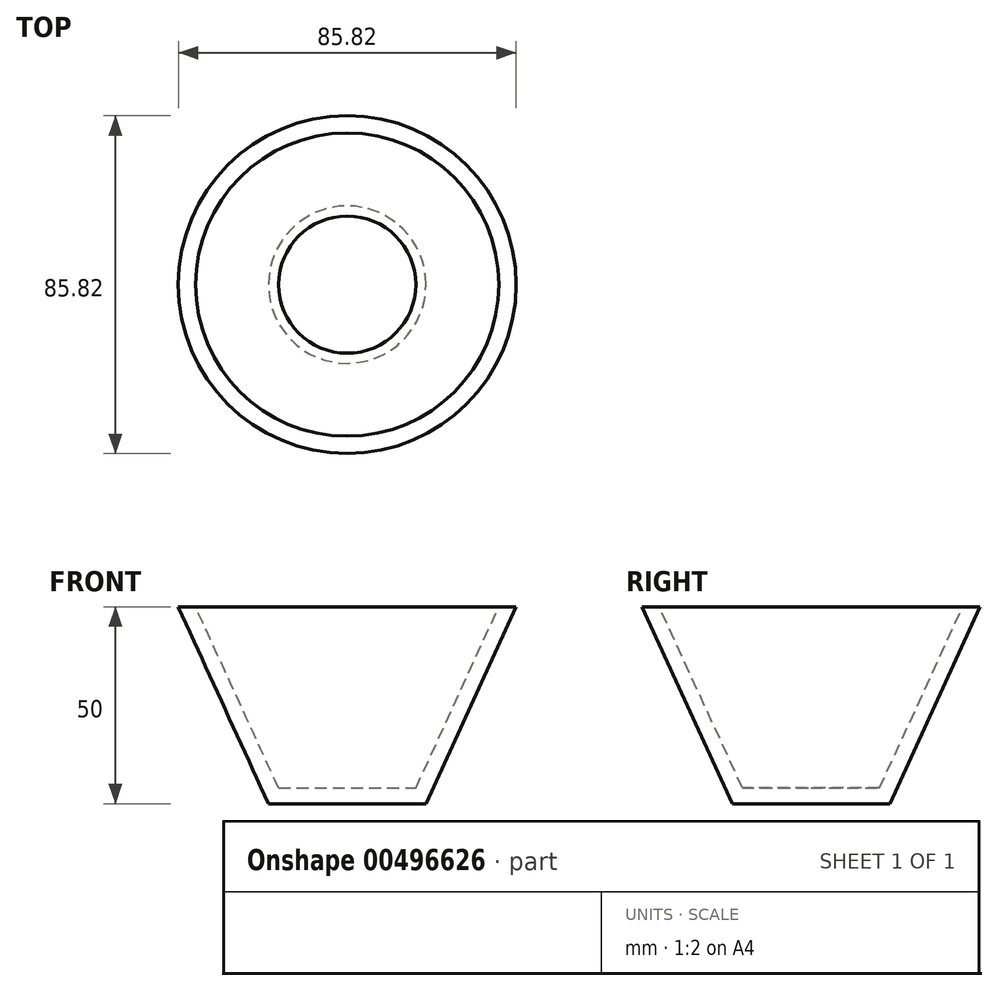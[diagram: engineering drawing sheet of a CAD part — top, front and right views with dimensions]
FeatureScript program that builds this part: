
annotation { "Feature Type Name" : "Feature", "Feature Type Description" : "" }
export const myFeature = defineFeature(function(context is Context, id is Id, definition is map)
    precondition{}
    {
        {
            var Q0;
            Q0=qCreatedBy(makeId("Front.planeOp"),FACE);
            var sketch = newSketch(context, id + "F0", { "sketchPlane" : qUnion([Q0])});
            skLineSegment(sketch, "E0", {"start": v(0, 0) * mm, "end": v(0, 50) * mm, "construction": true});
            skLineSegment(sketch, "E1", {"start": v(0, 0) * mm, "end": v(20, 0) * mm});
            skLineSegment(sketch, "E2", {"start": v(20, 0) * mm, "end": v(42.91, 50) * mm});
            skLineSegment(sketch, "E3.0", {"start": v(17.43, 4) * mm, "end": v(38.51, 50) * mm});
            skLineSegment(sketch, "E3.1", {"start": v(0, 4) * mm, "end": v(17.43, 4) * mm});
            skLineSegment(sketch, "E4", {"start": v(0, 4) * mm, "end": v(0, 0) * mm});
            skLineSegment(sketch, "E5", {"start": v(38.51, 50) * mm, "end": v(42.91, 50) * mm});
            skSolve(sketch);
        }
        {
            var Q0;
            Q0=makeQuery(id+"F0.imprint","IMPRINT",FACE,{"disambiguationData":[TD([[makeQuery(id+"F0.imprint","IMPRINT",EDGE,{"derivedFrom":sQuery(id+"F0.wireOp",EDGE,"E1")}),1.0]])]});
            var Q1;
            Q1=sQuery(id+"F0.wireOp",EDGE,"E0");
            revolve(context, id + "F1", {"entities" : qUnion([Q0]), "axis" : qUnion([Q1]), "revolveType" : RevolveType.FULL});
        }
    });
